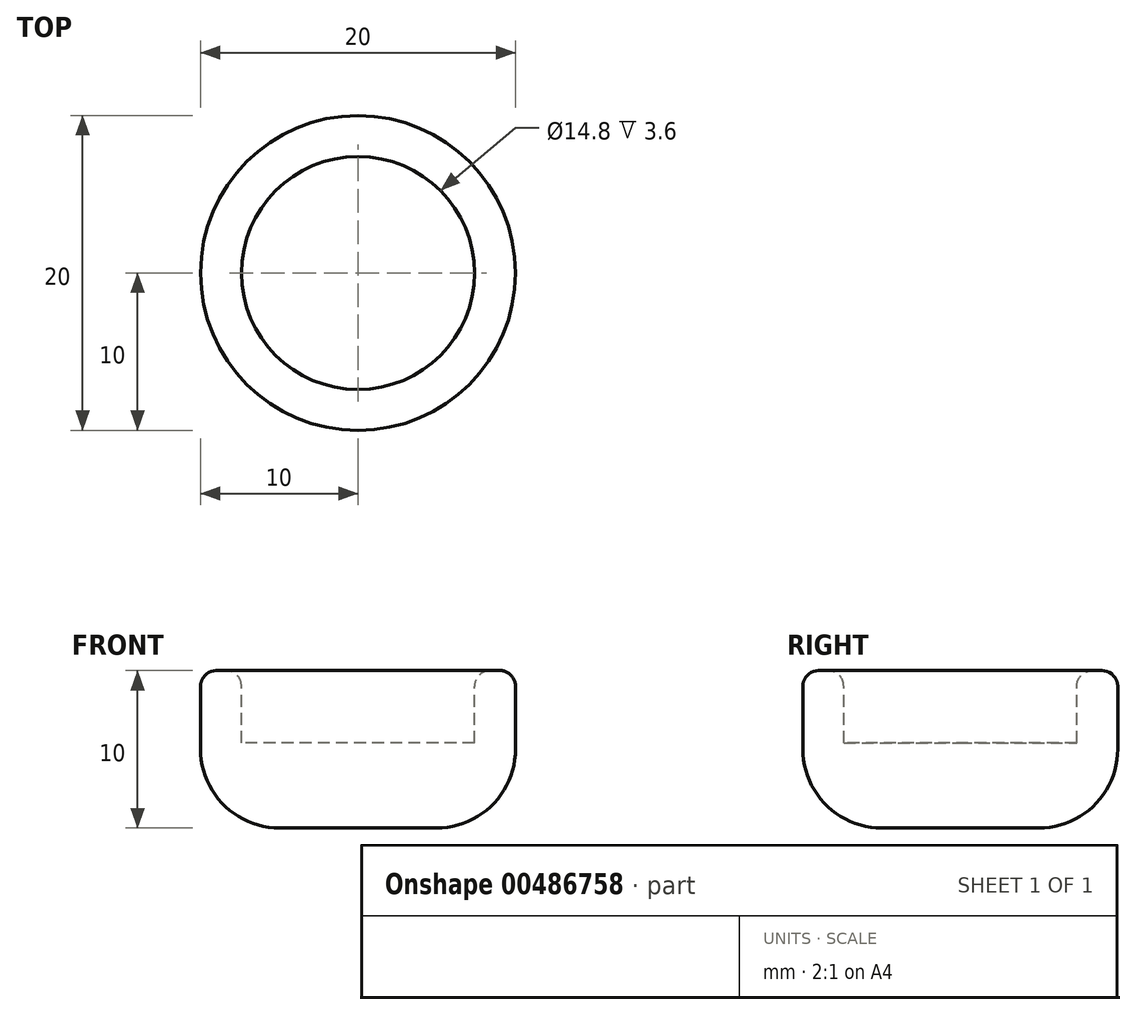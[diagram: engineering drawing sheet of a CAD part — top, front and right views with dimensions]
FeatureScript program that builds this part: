
annotation { "Feature Type Name" : "Feature", "Feature Type Description" : "" }
export const myFeature = defineFeature(function(context is Context, id is Id, definition is map)
    precondition{}
    {
        {
            var Q0;
            Q0=qCreatedBy(makeId("Top.planeOp"),FACE);
            var sketch = newSketch(context, id + "F0", { "sketchPlane" : qUnion([Q0])});
            skCircle(sketch, "E0", {"center": v(0, 0) * mm, "radius": 10 * mm});
            skSolve(sketch);
        }
        {
            var Q0;
            Q0 = qSketchRegion(id + "F0", true);
            extrude(context, id + "F1", {"entities" : qUnion([Q0]), "depth" : 10 * mm, "offsetDistance" : 25 * mm});
        }
        {
            var Q0;
            Q0=makeQuery(id+"F1.opExtrude","CAP_FACE",FACE,{"disambiguationData":[OSD([sQuery(id+"F0.wireOp",EDGE,"E0")])],"isStart":false});
            var sketch = newSketch(context, id + "F2", { "sketchPlane" : qUnion([Q0])});
            skCircle(sketch, "E1", {"center": v(0, 0) * mm, "radius": 7.4 * mm});
            skSolve(sketch);
        }
        {
            var Q0;
            Q0 = qSketchRegion(id + "F2", true);
            extrude(context, id + "F3", {"entities" : qUnion([Q0]), "operationType" : NewBodyOperationType.REMOVE, "oppositeDirection" : true, "depth" : 4.6 * mm, "offsetDistance" : 25 * mm});
        }
        {
            var Q0;
            Q0=makeQuery(id+"F1.opExtrude","CAP_EDGE",EDGE,{"disambiguationData":[OSD([sQuery(id+"F0.wireOp",EDGE,"E0")])],"isStart":true});
            fillet(context, id + "F4", {"entities" : qUnion([Q0]), "radius" : 5 * mm, "tangentPropagation" : true, "allowEdgeOverflow" : false});
        }
        {
            var Q0;
            Q0=makeQuery(id+"F3.boolean.opBoolean","COPY",EDGE,{"derivedFrom":makeQuery(id+"F3.opExtrude","CAP_EDGE",EDGE,{"disambiguationData":[OSD([sQuery(id+"F2.wireOp",EDGE,"E1")])],"isStart":true})});
            var Q1;
            Q1=makeQuery(id+"F1.opExtrude","CAP_FACE",FACE,{"disambiguationData":[OSD([sQuery(id+"F0.wireOp",EDGE,"E0")])],"isStart":false});
            fillet(context, id + "F5", {"entities" : qUnion([Q0, Q1]), "radius" : 1 * mm, "tangentPropagation" : true, "allowEdgeOverflow" : false});
        }
    });
